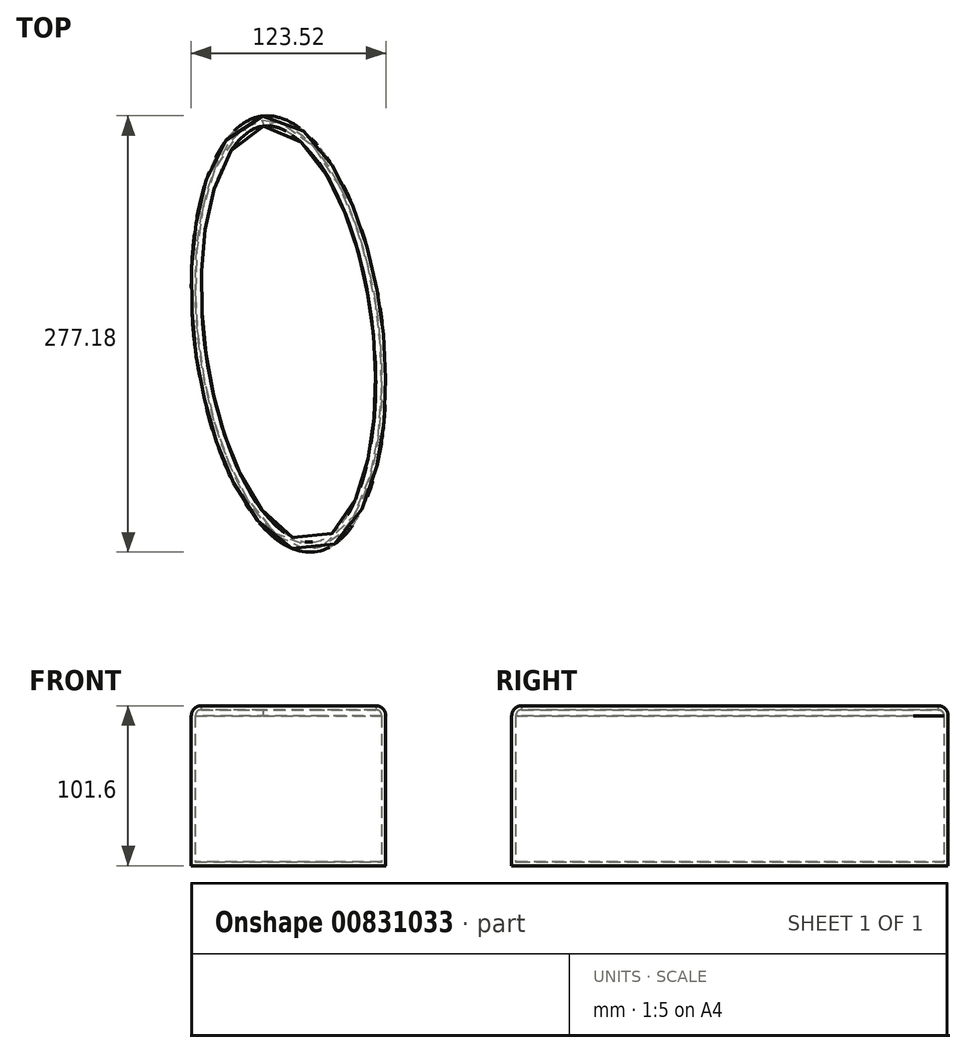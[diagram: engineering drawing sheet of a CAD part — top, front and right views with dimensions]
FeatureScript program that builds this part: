
annotation { "Feature Type Name" : "Feature", "Feature Type Description" : "" }
export const myFeature = defineFeature(function(context is Context, id is Id, definition is map)
    precondition{}
    {
        {
            var Q0;
            Q0=qCreatedBy(makeId("Top.planeOp"),FACE);
            var sketch = newSketch(context, id + "F0", { "sketchPlane" : qUnion([Q0])});
            skEllipse(sketch, "E0", {"center": v(0, 0) * mm, "majorRadius": 139.4 * mm, "minorRadius": 59.92 * mm, "majorAxis": v(-0.12, 1)});
            skSolve(sketch);
        }
        {
            var Q0;
            Q0 = qSketchRegion(id + "F0", true);
            extrude(context, id + "F1", {"entities" : qUnion([Q0]), "depth" : 101.6 * mm, "offsetDistance" : 25.4 * mm});
        }
        {
            var Q0;
            Q0=makeQuery(id+"F1.opExtrude","CAP_EDGE",EDGE,{"disambiguationData":[OSD([sQuery(id+"F0.wireOp",EDGE,"E0")])],"isStart":false});
            fillet(context, id + "F2", {"entities" : qUnion([Q0]), "radius" : 6.35 * mm, "tangentPropagation" : true, "allowEdgeOverflow" : false});
        }
        {
            var Q0;
            Q0=makeQuery(id+"F1.opExtrude","CAP_FACE",FACE,{"disambiguationData":[OSD([sQuery(id+"F0.wireOp",EDGE,"E0")])],"isStart":false});
            shell(context, id + "F3", {"entities" : qUnion([Q0]), "thickness" : 2.54 * mm});
        }
        {
            var Q0;
            Q0=qCreatedBy(makeId("Right.planeOp"),FACE);
            var sketch = newSketch(context, id + "F4", { "sketchPlane" : qUnion([Q0])});
            skPoint(sketch, "E1", {"position": v(-139.49, 41.98) * mm});
            skPoint(sketch, "E2", {"position": v(0, 99) * mm});
            skPoint(sketch, "E3", {"position": v(140.14, 41.98) * mm});
            skFitSpline(sketch, "E4", {"points": [v(-139.49, 41.98) * mm, v(0, 99) * mm, v(140.14, 41.98) * mm], "startDerivative": vector(279.07, 171.15) * mm, "endDerivative": vector(280.18, -171.04) * mm});
            skSolve(sketch);
        }
    });
